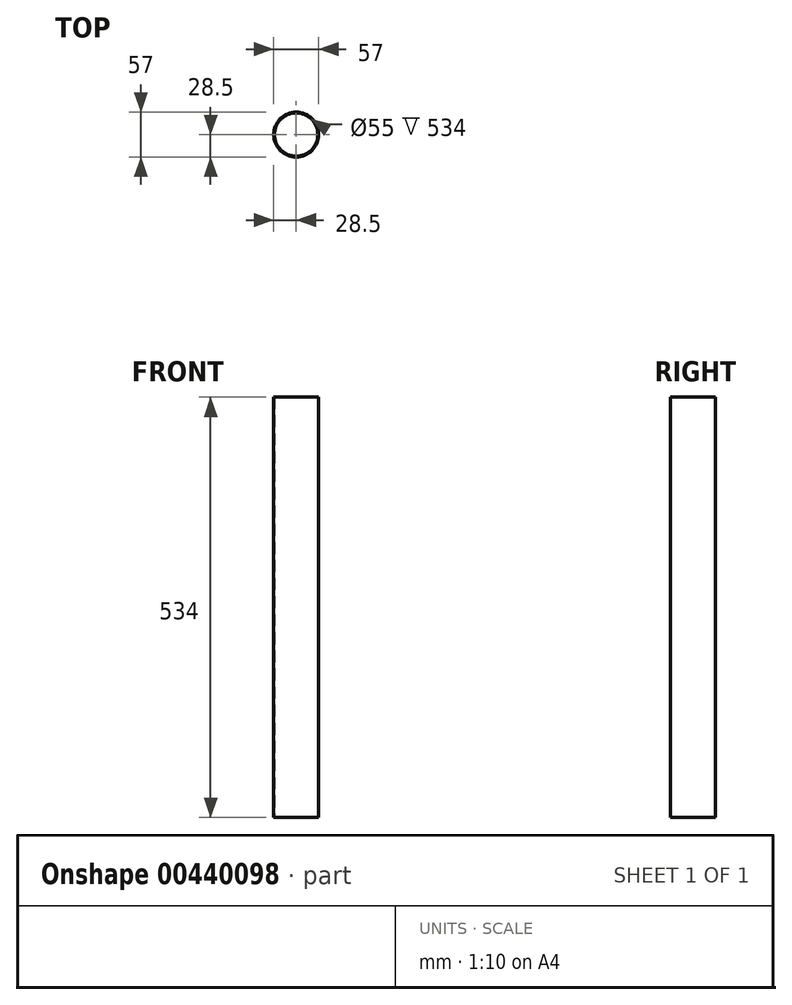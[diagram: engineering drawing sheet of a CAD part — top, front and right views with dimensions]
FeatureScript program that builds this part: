
annotation { "Feature Type Name" : "Feature", "Feature Type Description" : "" }
export const myFeature = defineFeature(function(context is Context, id is Id, definition is map)
    precondition{}
    {
        {
            var Q0;
            Q0=qCreatedBy(makeId("Top.planeOp"),FACE);
            var sketch = newSketch(context, id + "F0", { "sketchPlane" : qUnion([Q0])});
            skCircle(sketch, "E0", {"center": v(0, 0) * mm, "radius": 28.5 * mm});
            skCircle(sketch, "E1", {"center": v(0, 0) * mm, "radius": 27.5 * mm});
            skSolve(sketch);
        }
        {
            var Q0;
            Q0=makeQuery(id+"F0.imprint","IMPRINT",FACE,{"disambiguationData":[TD([[makeQuery(id+"F0.imprint","IMPRINT",EDGE,{"derivedFrom":sQuery(id+"F0.wireOp",EDGE,"E0")}),1.0]])]});
            extrude(context, id + "F1", {"entities" : qUnion([Q0]), "depth" : 534 * mm, "offsetDistance" : 25 * mm});
        }
    });
